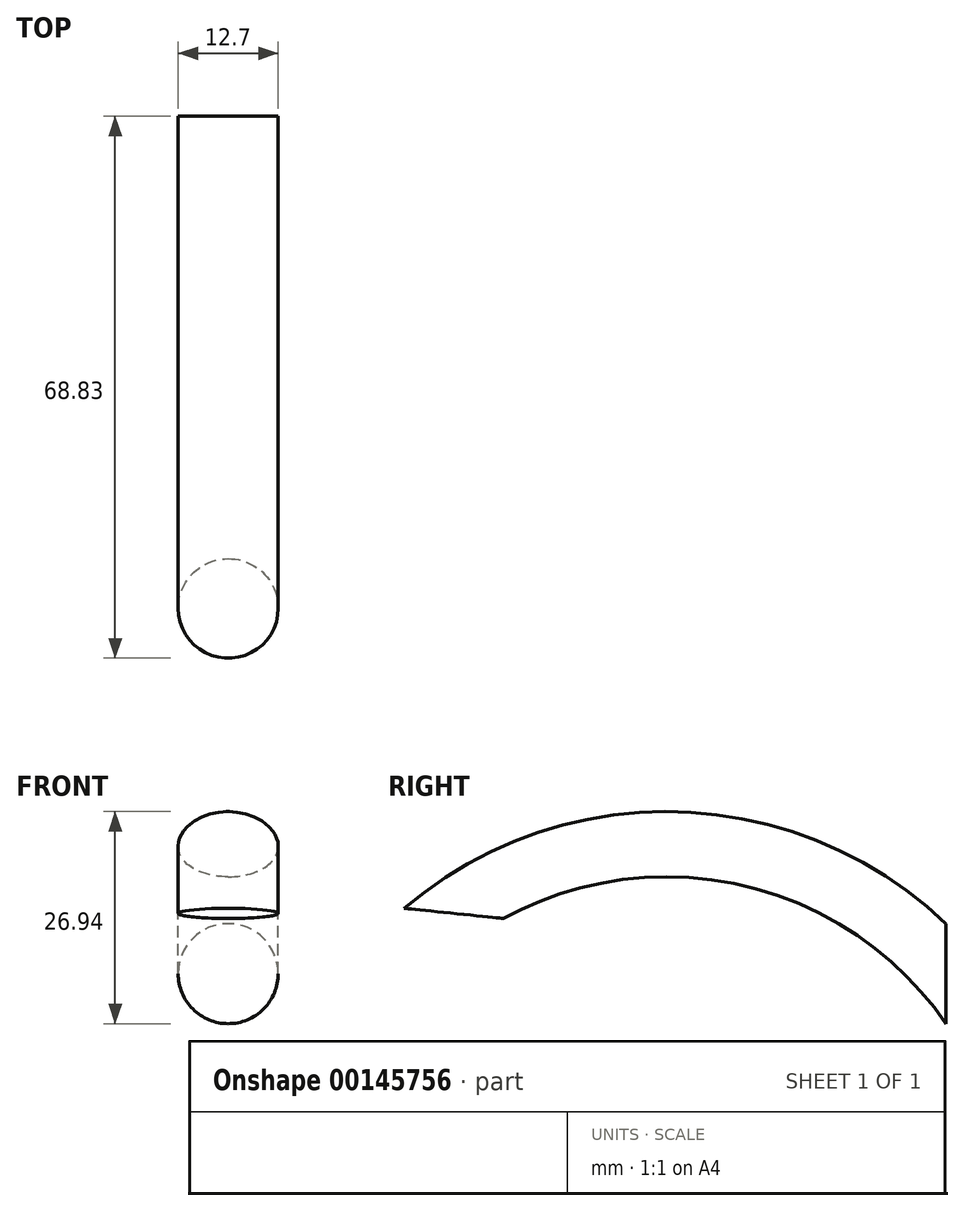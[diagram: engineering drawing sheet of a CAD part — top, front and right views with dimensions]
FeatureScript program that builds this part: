
annotation { "Feature Type Name" : "Feature", "Feature Type Description" : "" }
export const myFeature = defineFeature(function(context is Context, id is Id, definition is map)
    precondition{}
    {
        {
            var Q0;
            Q0=qCreatedBy(makeId("Front.planeOp"),FACE);
            var sketch = newSketch(context, id + "F0", { "sketchPlane" : qUnion([Q0])});
            skCircle(sketch, "E0", {"center": v(0, 21.58) * mm, "radius": 6.35 * mm});
            skLineSegment(sketch, "E1", {"start": v(0, 0) * mm, "end": v(0, 21.58) * mm, "construction": true});
            skSolve(sketch);
        }
        {
            var Q0;
            Q0=qCreatedBy(makeId("Right.planeOp"),FACE);
            var sketch = newSketch(context, id + "F1", { "sketchPlane" : qUnion([Q0])});
            skArc(sketch, "E2", {"start": v(0, 21.58) * mm, "mid": v(-29.78, 37.44) * mm, "end": v(-62.52, 29.24) * mm});
            skSolve(sketch);
        }
        {
            var Q0;
            Q0=makeQuery(id+"F0.imprint","IMPRINT",FACE,{"disambiguationData":[TD([[makeQuery(id+"F0.imprint","IMPRINT",EDGE,{"derivedFrom":sQuery(id+"F0.wireOp",EDGE,"E0")}),1.0]])]});
            var Q1;
            Q1=sQuery(id+"F1.wireOp",EDGE,"E2");
            sweep(context, id + "F2", {"profiles" : qUnion([Q0]), "path" : qUnion([Q1])});
        }
    });
